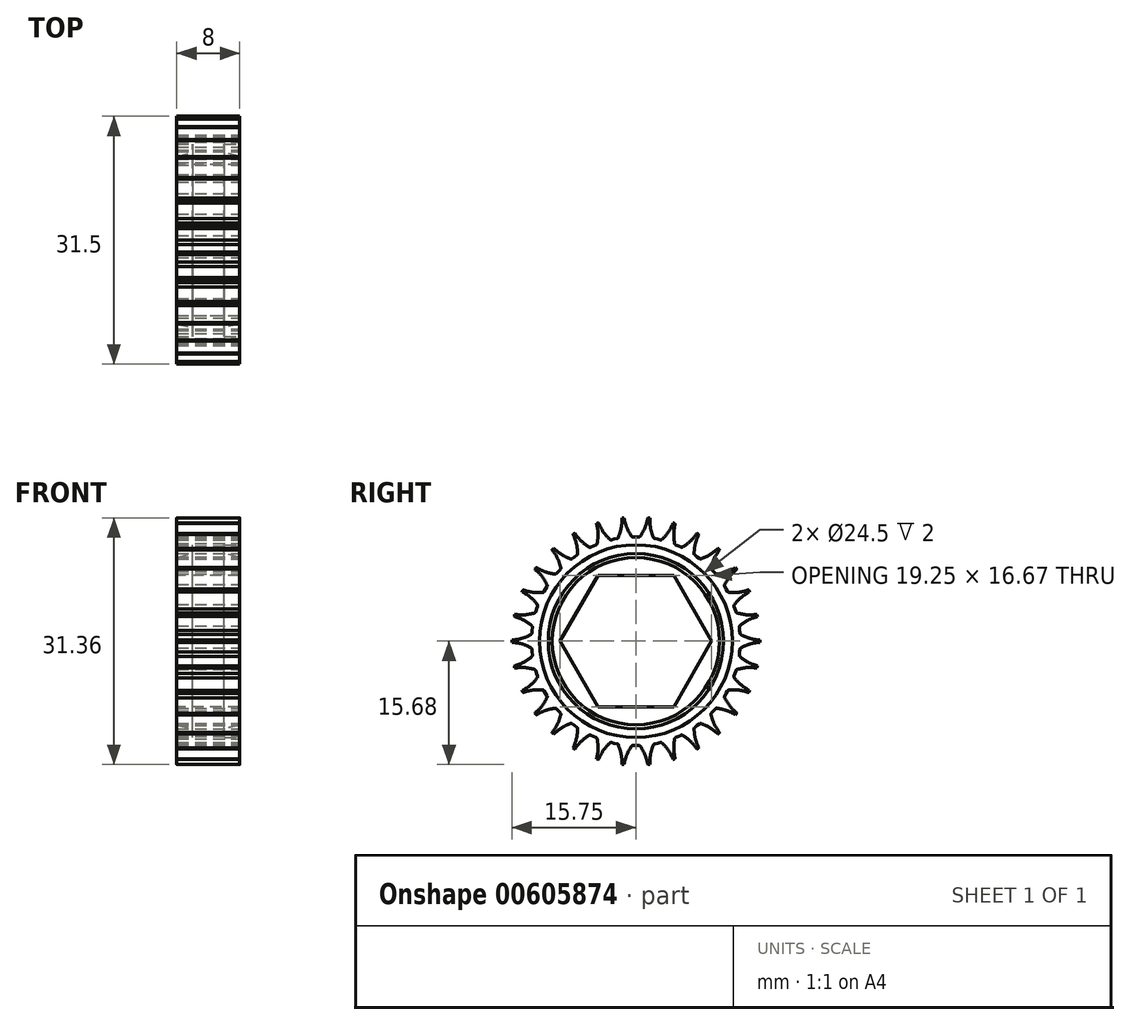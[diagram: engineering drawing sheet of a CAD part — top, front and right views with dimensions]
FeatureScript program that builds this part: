
annotation { "Feature Type Name" : "Feature", "Feature Type Description" : "" }
export const myFeature = defineFeature(function(context is Context, id is Id, definition is map)
    precondition{}
    {
        {
            var Q0;
            Q0=qCreatedBy(makeId("Front.planeOp"),FACE);
            var sketch = newSketch(context, id + "F0", { "sketchPlane" : qUnion([Q0])});
            skLineSegment(sketch, "E0", {"start": v(0, 9.62) * mm, "end": v(0, 15.75) * mm, "construction": true});
            skLineSegment(sketch, "E1", {"start": v(0, 15.75) * mm, "end": v(-4, 15.75) * mm});
            skLineSegment(sketch, "E2", {"start": v(-4, 15.75) * mm, "end": v(-4, 12.25) * mm});
            skLineSegment(sketch, "E3", {"start": v(-4, 0) * mm, "end": v(0, 0) * mm, "construction": true});
            skLineSegment(sketch, "E4", {"start": v(-4, 12.25) * mm, "end": v(-2, 12.25) * mm});
            skLineSegment(sketch, "E5", {"start": v(-2, 12.25) * mm, "end": v(-2, 11.13) * mm});
            skLineSegment(sketch, "E6", {"start": v(-4, 9.62) * mm, "end": v(0, 9.62) * mm});
            skLineSegment(sketch, "E7", {"start": v(-4, 9.62) * mm, "end": v(-4, 10.62) * mm});
            skLineSegment(sketch, "E8", {"start": v(-4, 10.62) * mm, "end": v(-2, 11.12) * mm});
            skLineSegment(sketch, "E9.trimOffspring", {"start": v(-4, 10.62) * mm, "end": v(-4, 9.62) * mm});
            skPoint(sketch, "E10.orphan", {"position": v(-4, 11.13) * mm});
            skLineSegment(sketch, "E11.MirrorCS", {"start": v(0, 15.75) * mm, "end": v(4, 15.75) * mm});
            skLineSegment(sketch, "E12.MirrorCS", {"start": v(4, 15.75) * mm, "end": v(4, 12.25) * mm});
            skLineSegment(sketch, "E13.MirrorCS", {"start": v(4, 12.25) * mm, "end": v(2, 12.25) * mm});
            skLineSegment(sketch, "E14.MirrorCS", {"start": v(2, 12.25) * mm, "end": v(2, 11.13) * mm});
            skLineSegment(sketch, "E15.MirrorCS", {"start": v(4, 10.62) * mm, "end": v(2, 11.12) * mm});
            skLineSegment(sketch, "E16.MirrorCS", {"start": v(4, 10.62) * mm, "end": v(4, 9.62) * mm});
            skLineSegment(sketch, "E17.MirrorCS", {"start": v(4, 9.62) * mm, "end": v(0, 9.62) * mm});
            skLineSegment(sketch, "E18", {"start": v(-4, 9.62) * mm, "end": v(-4, 0) * mm});
            skLineSegment(sketch, "E19", {"start": v(4, 9.62) * mm, "end": v(4, 0) * mm});
            skPoint(sketch, "E19.endSnap0", {"position": v(-2, 0) * mm});
            skLineSegment(sketch, "E20", {"start": v(4, 0) * mm, "end": v(-4, 0) * mm});
            skSolve(sketch);
        }
        {
            var Q0;
            Q0=makeQuery(id+"F0.imprint","IMPRINT",FACE,{"disambiguationData":[TD([[makeQuery(id+"F0.imprint","IMPRINT",EDGE,{"derivedFrom":sQuery(id+"F0.wireOp",EDGE,"E1")}),1.0]])]});
            var Q1;
            Q1=makeQuery(id+"F0.imprint","IMPRINT",FACE,{"disambiguationData":[TD([[makeQuery(id+"F0.imprint","IMPRINT",EDGE,{"derivedFrom":sQuery(id+"F0.wireOp",EDGE,"E6")}),-1.0]])]});
            var Q2;
            Q2=sQuery(id+"F0.wireOp",EDGE,"E20");
            revolve(context, id + "F1", {"entities" : qUnion([Q0, Q1]), "axis" : qUnion([Q2]), "revolveType" : RevolveType.FULL});
        }
        {
            var Q0;
            Q0=makeQuery(id+"F1.opRevolve","SWEPT_FACE",FACE,{"disambiguationData":[OSD([sQuery(id+"F0.wireOp",EDGE,"E9.trimOffspring"),sQuery(id+"F0.wireOp",EDGE,"E18")])]});
            var sketch = newSketch(context, id + "F2", { "sketchPlane" : qUnion([Q0])});
            skCircle(sketch, "E21.cCircle", {"center": v(0, 0) * mm, "radius": 8.34 * mm, "construction": true});
            skLineSegment(sketch, "E21.0", {"start": v(-4.81, 8.34) * mm, "end": v(4.81, 8.34) * mm});
            skLineSegment(sketch, "E21.1", {"start": v(4.81, 8.34) * mm, "end": v(9.63, 0) * mm});
            skLineSegment(sketch, "E21.2", {"start": v(9.63, 0) * mm, "end": v(4.81, -8.34) * mm});
            skLineSegment(sketch, "E21.3", {"start": v(4.81, -8.34) * mm, "end": v(-4.81, -8.34) * mm});
            skLineSegment(sketch, "E21.4", {"start": v(-4.81, -8.34) * mm, "end": v(-9.63, 0) * mm});
            skLineSegment(sketch, "E21.5", {"start": v(-9.62, 0) * mm, "end": v(-4.81, 8.34) * mm});
            skPoint(sketch, "E21.0.midPoint", {"position": v(0, 8.34) * mm});
            skSolve(sketch);
        }
        {
            var Q0;
            Q0=makeQuery(id+"F2.imprint","IMPRINT",FACE,{"disambiguationData":[TD([[makeQuery(id+"F2.imprint","IMPRINT",EDGE,{"derivedFrom":sQuery(id+"F2.wireOp",EDGE,"E21.0")}),-1.0]])]});
            extrude(context, id + "F3", {"entities" : qUnion([Q0]), "operationType" : NewBodyOperationType.REMOVE, "endBound" : BoundingType.THROUGH_ALL, "oppositeDirection" : true, "depth" : 25 * mm, "offsetDistance" : 25 * mm});
        }
        {
            var Q0;
            Q0=qCreatedBy(makeId("Right.planeOp"),FACE);
            var sketch = newSketch(context, id + "F4", { "sketchPlane" : qUnion([Q0])});
            skFitSpline(sketch, "E22", {"points": [v(0.5, 13.24) * mm, v(1.2, 14.5) * mm, v(1.52, 15.73) * mm], "startDerivative": vector(1.5, 2.42) * mm, "endDerivative": vector(0.48, 2.47) * mm});
            skArc(sketch, "E23.filletArc", {"start": v(0.36, 13.24) * mm, "mid": v(0.48, 13.27) * mm, "end": v(0.58, 13.36) * mm});
            skLineSegment(sketch, "E24.MirrorCS", {"start": v(0, 15.78) * mm, "end": v(-1.52, 15.73) * mm});
            skFitSpline(sketch, "E25.MirrorCS", {"points": [v(-0.5, 13.24) * mm, v(-1.2, 14.5) * mm, v(-1.52, 15.73) * mm], "startDerivative": vector(-1.5, 2.42) * mm, "endDerivative": vector(-0.48, 2.47) * mm});
            skArc(sketch, "E26.MirrorCS", {"start": v(-0.36, 13.24) * mm, "mid": v(-0.48, 13.27) * mm, "end": v(-0.58, 13.36) * mm});
            skLineSegment(sketch, "E27.MirrorCS", {"start": v(0, 13.25) * mm, "end": v(-0.36, 13.24) * mm});
            skLineSegment(sketch, "E28", {"start": v(0, 0) * mm, "end": v(0, 15.75) * mm, "construction": true});
            skLineSegment(sketch, "E29.MirrorCS", {"start": v(0, 13.25) * mm, "end": v(0.36, 13.24) * mm});
            skLineSegment(sketch, "E30.MirrorCS", {"start": v(0, 15.78) * mm, "end": v(1.52, 15.73) * mm});
            skSolve(sketch);
        }
        {
            var Q0;
            Q0 = qSketchRegion(id + "F4", true);
            extrude(context, id + "F5", {"entities" : qUnion([Q0]), "operationType" : NewBodyOperationType.REMOVE, "oppositeDirection" : true, "depth" : 8 * mm, "offsetDistance" : 25 * mm, "symmetric" : true});
        }
        {
            var Q0;
            Q0=makeQuery(id+"F5.boolean.opBoolean","COPY",FACE,{"derivedFrom":makeQuery(id+"F5.opExtrude","SWEPT_FACE",FACE,{"disambiguationData":[OSD([sQuery(id+"F4.wireOp",EDGE,"E25.MirrorCS")])]})});
            var Q1;
            Q1=makeQuery(id+"F5.boolean.opBoolean","COPY",FACE,{"derivedFrom":makeQuery(id+"F5.opExtrude","SWEPT_FACE",FACE,{"disambiguationData":[OSD([sQuery(id+"F4.wireOp",EDGE,"E26.MirrorCS")])]})});
            var Q2;
            Q2=makeQuery(id+"F5.boolean.opBoolean","COPY",FACE,{"derivedFrom":makeQuery(id+"F5.opExtrude","SWEPT_FACE",FACE,{"disambiguationData":[OSD([sQuery(id+"F4.wireOp",EDGE,"E27.MirrorCS")])]})});
            var Q3;
            Q3=makeQuery(id+"F5.boolean.opBoolean","COPY",FACE,{"derivedFrom":makeQuery(id+"F5.opExtrude","SWEPT_FACE",FACE,{"disambiguationData":[OSD([sQuery(id+"F4.wireOp",EDGE,"E29.MirrorCS")])]})});
            var Q4;
            Q4=makeQuery(id+"F5.boolean.opBoolean","COPY",FACE,{"derivedFrom":makeQuery(id+"F5.opExtrude","SWEPT_FACE",FACE,{"disambiguationData":[OSD([sQuery(id+"F4.wireOp",EDGE,"E23.filletArc")])]})});
            var Q5;
            Q5=makeQuery(id+"F5.boolean.opBoolean","COPY",FACE,{"derivedFrom":makeQuery(id+"F5.opExtrude","SWEPT_FACE",FACE,{"disambiguationData":[OSD([sQuery(id+"F4.wireOp",EDGE,"E22")])]})});
            var Q6;
            Q6=makeQuery(id+"F1.opRevolve","SWEPT_FACE",FACE,{"disambiguationData":[OSD([sQuery(id+"F0.wireOp",EDGE,"E1"),sQuery(id+"F0.wireOp",EDGE,"E11.MirrorCS")])]});
            circularPattern(context, id + "F6", {"patternType" : PatternType.FACE, "faces" : qUnion([Q0, Q1, Q2, Q3, Q4, Q5]), "axis" : qUnion([Q6]), "angle" : 360 * degree, "instanceCount" : 30, "equalSpace" : true});
        }
    });
